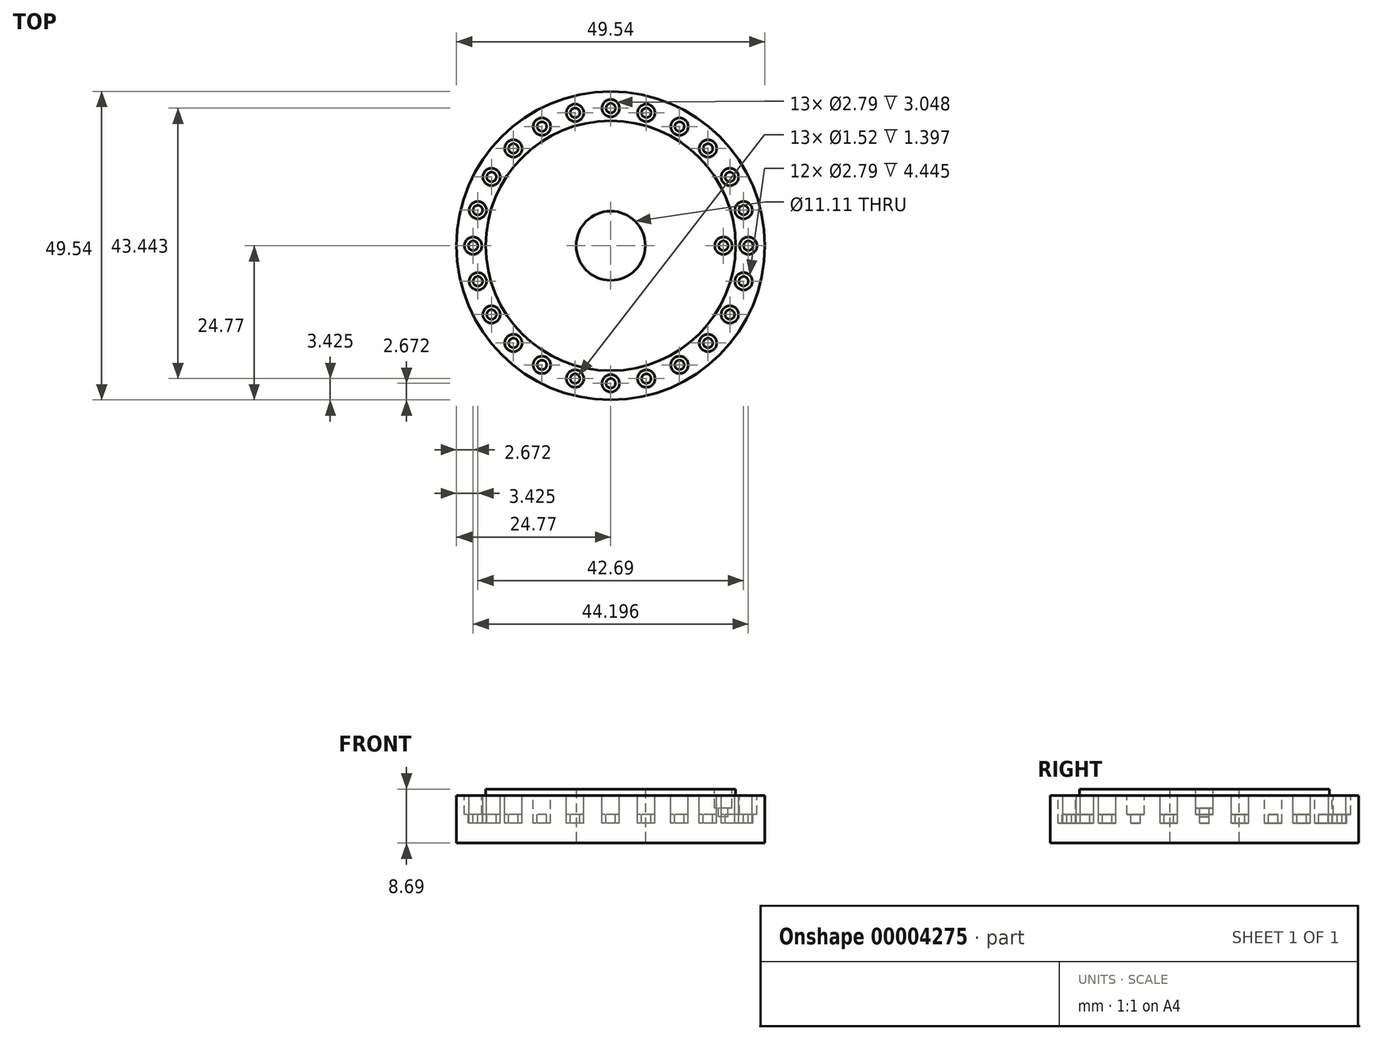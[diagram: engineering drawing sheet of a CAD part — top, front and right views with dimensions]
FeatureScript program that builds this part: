
annotation { "Feature Type Name" : "Feature", "Feature Type Description" : "" }
export const myFeature = defineFeature(function(context is Context, id is Id, definition is map)
    precondition{}
    {
        {
            var Q0;
            Q0=qCreatedBy(makeId("Top.planeOp"),FACE);
            var sketch = newSketch(context, id + "F0", { "sketchPlane" : qUnion([Q0])});
            skCircle(sketch, "E0", {"center": v(0, 0) * mm, "radius": 24.77 * mm});
            skCircle(sketch, "E1", {"center": v(0, 0) * mm, "radius": 20.07 * mm});
            skCircle(sketch, "E2", {"center": v(0, 0) * mm, "radius": 5.56 * mm});
            skSolve(sketch);
        }
        {
            var Q0;
            Q0=makeQuery(id+"F0.imprint","IMPRINT",FACE,{"disambiguationData":[TD([[makeQuery(id+"F0.imprint","IMPRINT",EDGE,{"derivedFrom":sQuery(id+"F0.wireOp",EDGE,"E1")}),1.0]])]});
            extrude(context, id + "F1", {"entities" : qUnion([Q0]), "depth" : 8.7 * mm});
        }
        {
            var Q0;
            Q0=makeQuery(id+"F0.imprint","IMPRINT",FACE,{"disambiguationData":[TD([[makeQuery(id+"F0.imprint","IMPRINT",EDGE,{"derivedFrom":sQuery(id+"F0.wireOp",EDGE,"E0")}),1.0]])]});
            extrude(context, id + "F2", {"entities" : qUnion([Q0]), "operationType" : NewBodyOperationType.ADD, "depth" : 7.62 * mm});
        }
        {
            var Q0;
            Q0=makeQuery(id+"F1.opExtrude","CAP_FACE",FACE,{"disambiguationData":[OSD([sQuery(id+"F0.wireOp",EDGE,"E1"),sQuery(id+"F0.wireOp",EDGE,"E2")])],"isStart":false});
            var sketch = newSketch(context, id + "F3", { "sketchPlane" : qUnion([Q0])});
            skLineSegment(sketch, "E3", {"start": v(0, 0) * mm, "end": v(16.71, 0) * mm});
            skCircle(sketch, "E4", {"center": v(18.11, 0) * mm, "radius": 0.76 * mm});
            skLineSegment(sketch, "E5.trimOffspring", {"start": v(19.5, 0) * mm, "end": v(20.07, 0) * mm});
            skCircle(sketch, "E6", {"center": v(18.11, 0) * mm, "radius": 1.4 * mm});
            skSolve(sketch);
        }
        {
            var Q0;
            {var subQ0=sQuery(id+"F3.wireOp",EDGE,"E4");var subQ2=makeQuery(id+"F3.imprint","INTERSECT",VERTEX,{"derivedFrom":[sQuery(id+"F3.wireOp",EDGE,"E3"),subQ0]});Q0=makeQuery(id+"F3.imprint","IMPRINT",FACE,{"disambiguationData":[TD([[makeQuery(id+"F3.imprint","IMPRINT",EDGE,{"disambiguationData":[TD([[subQ2,1.0]])],"derivedFrom":subQ0}),1.0]])]});}
            var Q1;
            Q1 = qSketchRegion(id + "F5", true);
            extrude(context, id + "F4", {"entities" : qUnion([Q0, Q1]), "operationType" : NewBodyOperationType.REMOVE, "oppositeDirection" : true, "depth" : 4.44 * mm});
        }
        {
            var Q0;
            Q0=makeQuery(id+"F2.opExtrude","CAP_FACE",FACE,{"disambiguationData":[OSD([sQuery(id+"F0.wireOp",EDGE,"E0"),sQuery(id+"F0.wireOp",EDGE,"E1")])],"isStart":false});
            var sketch = newSketch(context, id + "F5", { "sketchPlane" : qUnion([Q0])});
            skLineSegment(sketch, "E7", {"start": v(0, 0) * mm, "end": v(21.34, 0) * mm, "construction": true});
            skLineSegment(sketch, "E8", {"start": v(0, 0) * mm, "end": v(20.6, 5.52) * mm, "construction": true});
            skCircle(sketch, "E9", {"center": v(22.1, 0) * mm, "radius": 0.76 * mm});
            skCircle(sketch, "E10", {"center": v(21.35, 5.72) * mm, "radius": 0.76 * mm});
            skCircle(sketch, "E11.0.MirrorC", {"center": v(19.14, 11.05) * mm, "radius": 0.76 * mm});
            skLineSegment(sketch, "E12", {"start": v(0, 0) * mm, "end": v(18.48, 10.67) * mm, "construction": true});
            skCircle(sketch, "E13.0.MirrorC", {"center": v(15.63, 15.63) * mm, "radius": 0.76 * mm});
            skCircle(sketch, "E14.0.MirrorC", {"center": v(11.05, 19.14) * mm, "radius": 0.76 * mm});
            skLineSegment(sketch, "E15", {"start": v(0, 0) * mm, "end": v(10.67, 18.48) * mm, "construction": true});
            skCircle(sketch, "E16.0.MirrorC", {"center": v(5.72, 21.35) * mm, "radius": 0.76 * mm});
            skCircle(sketch, "E17.0.MirrorC", {"center": v(0, 22.1) * mm, "radius": 0.76 * mm});
            skCircle(sketch, "E18.0.MirrorC", {"center": v(-5.72, 21.35) * mm, "radius": 0.76 * mm});
            skCircle(sketch, "E19.0.MirrorC", {"center": v(-11.05, 19.14) * mm, "radius": 0.76 * mm});
            skLineSegment(sketch, "E20", {"start": v(0, 0) * mm, "end": v(-10.67, 18.48) * mm, "construction": true});
            skCircle(sketch, "E21.0.MirrorC", {"center": v(-15.63, 15.63) * mm, "radius": 0.76 * mm});
            skCircle(sketch, "E22.0.MirrorC", {"center": v(-19.14, 11.05) * mm, "radius": 0.76 * mm});
            skCircle(sketch, "E23.0.MirrorC", {"center": v(-21.35, 5.72) * mm, "radius": 0.76 * mm});
            skCircle(sketch, "E24.0.MirrorC", {"center": v(-22.1, 0) * mm, "radius": 0.76 * mm});
            skCircle(sketch, "E25.0.MirrorC", {"center": v(-21.35, -5.72) * mm, "radius": 0.76 * mm});
            skCircle(sketch, "E26.0.MirrorC", {"center": v(-19.14, -11.05) * mm, "radius": 0.76 * mm});
            skCircle(sketch, "E27.0.MirrorC", {"center": v(-15.63, -15.63) * mm, "radius": 0.76 * mm});
            skCircle(sketch, "E28.0.MirrorC", {"center": v(-11.05, -19.14) * mm, "radius": 0.76 * mm});
            skCircle(sketch, "E29.0.MirrorC", {"center": v(21.35, -5.72) * mm, "radius": 0.76 * mm});
            skCircle(sketch, "E30.0.MirrorC", {"center": v(19.14, -11.05) * mm, "radius": 0.76 * mm});
            skCircle(sketch, "E31.0.MirrorC", {"center": v(15.63, -15.63) * mm, "radius": 0.76 * mm});
            skCircle(sketch, "E32.0.MirrorC", {"center": v(11.05, -19.14) * mm, "radius": 0.76 * mm});
            skCircle(sketch, "E33.0.MirrorC", {"center": v(5.72, -21.35) * mm, "radius": 0.76 * mm});
            skCircle(sketch, "E34.0.MirrorC", {"center": v(0, -22.1) * mm, "radius": 0.76 * mm});
            skCircle(sketch, "E35.0.MirrorC", {"center": v(-5.72, -21.35) * mm, "radius": 0.76 * mm});
            skLineSegment(sketch, "E36.trimOffspring", {"start": v(22.08, 5.92) * mm, "end": v(23.92, 6.4) * mm, "construction": true});
            skLineSegment(sketch, "E37.trimOffspring", {"start": v(22.86, 0) * mm, "end": v(24.77, 0) * mm, "construction": true});
            skCircle(sketch, "E38", {"center": v(22.1, 0) * mm, "radius": 1.4 * mm});
            skCircle(sketch, "E39", {"center": v(21.35, 5.72) * mm, "radius": 1.4 * mm});
            skCircle(sketch, "E40", {"center": v(19.14, 11.05) * mm, "radius": 1.4 * mm});
            skCircle(sketch, "E41", {"center": v(15.63, 15.63) * mm, "radius": 1.4 * mm});
            skCircle(sketch, "E42", {"center": v(11.05, 19.14) * mm, "radius": 1.4 * mm});
            skCircle(sketch, "E43", {"center": v(5.72, 21.35) * mm, "radius": 1.4 * mm});
            skCircle(sketch, "E44", {"center": v(0, 22.1) * mm, "radius": 1.4 * mm});
            skCircle(sketch, "E45", {"center": v(-5.72, 21.35) * mm, "radius": 1.4 * mm});
            skCircle(sketch, "E46", {"center": v(-11.05, 19.14) * mm, "radius": 1.4 * mm});
            skCircle(sketch, "E47", {"center": v(-15.63, 15.63) * mm, "radius": 1.4 * mm});
            skCircle(sketch, "E48", {"center": v(-19.14, 11.05) * mm, "radius": 1.4 * mm});
            skCircle(sketch, "E49", {"center": v(-21.35, 5.72) * mm, "radius": 1.4 * mm});
            skCircle(sketch, "E50", {"center": v(-22.1, 0) * mm, "radius": 1.4 * mm});
            skCircle(sketch, "E51", {"center": v(-21.35, -5.72) * mm, "radius": 1.4 * mm});
            skCircle(sketch, "E52", {"center": v(-19.14, -11.05) * mm, "radius": 1.4 * mm});
            skCircle(sketch, "E53", {"center": v(-15.63, -15.63) * mm, "radius": 1.4 * mm});
            skCircle(sketch, "E54", {"center": v(-11.05, -19.14) * mm, "radius": 1.4 * mm});
            skCircle(sketch, "E55", {"center": v(-5.72, -21.35) * mm, "radius": 1.4 * mm});
            skCircle(sketch, "E56", {"center": v(0, -22.1) * mm, "radius": 1.4 * mm});
            skCircle(sketch, "E57", {"center": v(5.72, -21.35) * mm, "radius": 1.4 * mm});
            skCircle(sketch, "E58", {"center": v(11.05, -19.14) * mm, "radius": 1.4 * mm});
            skCircle(sketch, "E59", {"center": v(15.63, -15.63) * mm, "radius": 1.4 * mm});
            skCircle(sketch, "E60", {"center": v(19.14, -11.05) * mm, "radius": 1.4 * mm});
            skCircle(sketch, "E61", {"center": v(21.35, -5.72) * mm, "radius": 1.4 * mm});
            skSolve(sketch);
        }
        {
            var Q0;
            Q0=makeQuery(id+"F5.imprint","IMPRINT",FACE,{"disambiguationData":[TD([[makeQuery(id+"F5.imprint","IMPRINT",EDGE,{"derivedFrom":sQuery(id+"F5.wireOp",EDGE,"E9")}),1.0]])]});
            var Q1;
            Q1=makeQuery(id+"F5.imprint","IMPRINT",FACE,{"disambiguationData":[TD([[makeQuery(id+"F5.imprint","IMPRINT",EDGE,{"derivedFrom":sQuery(id+"F5.wireOp",EDGE,"E10")}),1.0]])]});
            var Q2;
            Q2=makeQuery(id+"F5.imprint","IMPRINT",FACE,{"disambiguationData":[TD([[makeQuery(id+"F5.imprint","IMPRINT",EDGE,{"derivedFrom":sQuery(id+"F5.wireOp",EDGE,"E11.0.MirrorC")}),-1.0]])]});
            var Q3;
            Q3=makeQuery(id+"F5.imprint","IMPRINT",FACE,{"disambiguationData":[TD([[makeQuery(id+"F5.imprint","IMPRINT",EDGE,{"derivedFrom":sQuery(id+"F5.wireOp",EDGE,"E13.0.MirrorC")}),-1.0]])]});
            var Q4;
            Q4=makeQuery(id+"F5.imprint","IMPRINT",FACE,{"disambiguationData":[TD([[makeQuery(id+"F5.imprint","IMPRINT",EDGE,{"derivedFrom":sQuery(id+"F5.wireOp",EDGE,"E14.0.MirrorC")}),-1.0]])]});
            var Q5;
            Q5=makeQuery(id+"F5.imprint","IMPRINT",FACE,{"disambiguationData":[TD([[makeQuery(id+"F5.imprint","IMPRINT",EDGE,{"derivedFrom":sQuery(id+"F5.wireOp",EDGE,"E16.0.MirrorC")}),1.0]])]});
            var Q6;
            Q6=makeQuery(id+"F5.imprint","IMPRINT",FACE,{"disambiguationData":[TD([[makeQuery(id+"F5.imprint","IMPRINT",EDGE,{"derivedFrom":sQuery(id+"F5.wireOp",EDGE,"E17.0.MirrorC")}),1.0]])]});
            var Q7;
            Q7=makeQuery(id+"F5.imprint","IMPRINT",FACE,{"disambiguationData":[TD([[makeQuery(id+"F5.imprint","IMPRINT",EDGE,{"derivedFrom":sQuery(id+"F5.wireOp",EDGE,"E18.0.MirrorC")}),-1.0]])]});
            var Q8;
            Q8=makeQuery(id+"F5.imprint","IMPRINT",FACE,{"disambiguationData":[TD([[makeQuery(id+"F5.imprint","IMPRINT",EDGE,{"derivedFrom":sQuery(id+"F5.wireOp",EDGE,"E19.0.MirrorC")}),-1.0]])]});
            var Q9;
            Q9=makeQuery(id+"F5.imprint","IMPRINT",FACE,{"disambiguationData":[TD([[makeQuery(id+"F5.imprint","IMPRINT",EDGE,{"derivedFrom":sQuery(id+"F5.wireOp",EDGE,"E21.0.MirrorC")}),1.0]])]});
            var Q10;
            Q10=makeQuery(id+"F5.imprint","IMPRINT",FACE,{"disambiguationData":[TD([[makeQuery(id+"F5.imprint","IMPRINT",EDGE,{"derivedFrom":sQuery(id+"F5.wireOp",EDGE,"E22.0.MirrorC")}),-1.0]])]});
            var Q11;
            Q11=makeQuery(id+"F5.imprint","IMPRINT",FACE,{"disambiguationData":[TD([[makeQuery(id+"F5.imprint","IMPRINT",EDGE,{"derivedFrom":sQuery(id+"F5.wireOp",EDGE,"E23.0.MirrorC")}),-1.0]])]});
            var Q12;
            Q12=makeQuery(id+"F5.imprint","IMPRINT",FACE,{"disambiguationData":[TD([[makeQuery(id+"F5.imprint","IMPRINT",EDGE,{"derivedFrom":sQuery(id+"F5.wireOp",EDGE,"E24.0.MirrorC")}),1.0]])]});
            var Q13;
            Q13=makeQuery(id+"F5.imprint","IMPRINT",FACE,{"disambiguationData":[TD([[makeQuery(id+"F5.imprint","IMPRINT",EDGE,{"derivedFrom":sQuery(id+"F5.wireOp",EDGE,"E25.0.MirrorC")}),1.0]])]});
            var Q14;
            Q14=makeQuery(id+"F5.imprint","IMPRINT",FACE,{"disambiguationData":[TD([[makeQuery(id+"F5.imprint","IMPRINT",EDGE,{"derivedFrom":sQuery(id+"F5.wireOp",EDGE,"E26.0.MirrorC")}),1.0]])]});
            var Q15;
            Q15=makeQuery(id+"F5.imprint","IMPRINT",FACE,{"disambiguationData":[TD([[makeQuery(id+"F5.imprint","IMPRINT",EDGE,{"derivedFrom":sQuery(id+"F5.wireOp",EDGE,"E27.0.MirrorC")}),-1.0]])]});
            var Q16;
            Q16=makeQuery(id+"F5.imprint","IMPRINT",FACE,{"disambiguationData":[TD([[makeQuery(id+"F5.imprint","IMPRINT",EDGE,{"derivedFrom":sQuery(id+"F5.wireOp",EDGE,"E28.0.MirrorC")}),-1.0]])]});
            var Q17;
            Q17=makeQuery(id+"F5.imprint","IMPRINT",FACE,{"disambiguationData":[TD([[makeQuery(id+"F5.imprint","IMPRINT",EDGE,{"derivedFrom":sQuery(id+"F5.wireOp",EDGE,"E35.0.MirrorC")}),1.0]])]});
            var Q18;
            Q18=makeQuery(id+"F5.imprint","IMPRINT",FACE,{"disambiguationData":[TD([[makeQuery(id+"F5.imprint","IMPRINT",EDGE,{"derivedFrom":sQuery(id+"F5.wireOp",EDGE,"E34.0.MirrorC")}),-1.0]])]});
            var Q19;
            Q19=makeQuery(id+"F5.imprint","IMPRINT",FACE,{"disambiguationData":[TD([[makeQuery(id+"F5.imprint","IMPRINT",EDGE,{"derivedFrom":sQuery(id+"F5.wireOp",EDGE,"E33.0.MirrorC")}),-1.0]])]});
            var Q20;
            Q20=makeQuery(id+"F5.imprint","IMPRINT",FACE,{"disambiguationData":[TD([[makeQuery(id+"F5.imprint","IMPRINT",EDGE,{"derivedFrom":sQuery(id+"F5.wireOp",EDGE,"E32.0.MirrorC")}),1.0]])]});
            var Q21;
            Q21=makeQuery(id+"F5.imprint","IMPRINT",FACE,{"disambiguationData":[TD([[makeQuery(id+"F5.imprint","IMPRINT",EDGE,{"derivedFrom":sQuery(id+"F5.wireOp",EDGE,"E31.0.MirrorC")}),1.0]])]});
            var Q22;
            Q22=makeQuery(id+"F5.imprint","IMPRINT",FACE,{"disambiguationData":[TD([[makeQuery(id+"F5.imprint","IMPRINT",EDGE,{"derivedFrom":sQuery(id+"F5.wireOp",EDGE,"E30.0.MirrorC")}),1.0]])]});
            var Q23;
            Q23=makeQuery(id+"F5.imprint","IMPRINT",FACE,{"disambiguationData":[TD([[makeQuery(id+"F5.imprint","IMPRINT",EDGE,{"derivedFrom":sQuery(id+"F5.wireOp",EDGE,"E29.0.MirrorC")}),-1.0]])]});
            extrude(context, id + "F6", {"entities" : qUnion([Q0, Q1, Q2, Q3, Q4, Q5, Q6, Q7, Q8, Q9, Q10, Q11, Q12, Q13, Q14, Q15, Q16, Q17, Q18, Q19, Q20, Q21, Q22, Q23]), "operationType" : NewBodyOperationType.REMOVE, "oppositeDirection" : true, "depth" : 4.44 * mm});
        }
        {
            var Q0;
            Q0=qSketchRegion(id+"F3",true);
            extrude(context, id + "F7", {"entities" : qUnion([Q0]), "operationType" : NewBodyOperationType.REMOVE, "oppositeDirection" : true, "depth" : 3.05 * mm});
        }
        {
            var Q0;
            Q0=makeQuery(id+"F5.imprint","IMPRINT",FACE,{"disambiguationData":[TD([[makeQuery(id+"F5.imprint","IMPRINT",EDGE,{"derivedFrom":sQuery(id+"F5.wireOp",EDGE,"E9")}),-1.0]])]});
            var Q1;
            Q1=makeQuery(id+"F5.imprint","IMPRINT",FACE,{"disambiguationData":[TD([[makeQuery(id+"F5.imprint","IMPRINT",EDGE,{"derivedFrom":sQuery(id+"F5.wireOp",EDGE,"E10")}),-1.0]])]});
            var Q2;
            Q2=makeQuery(id+"F5.imprint","IMPRINT",FACE,{"disambiguationData":[TD([[makeQuery(id+"F5.imprint","IMPRINT",EDGE,{"derivedFrom":sQuery(id+"F5.wireOp",EDGE,"E29.0.MirrorC")}),1.0]])]});
            var Q3;
            Q3=makeQuery(id+"F5.imprint","IMPRINT",FACE,{"disambiguationData":[TD([[makeQuery(id+"F5.imprint","IMPRINT",EDGE,{"derivedFrom":sQuery(id+"F5.wireOp",EDGE,"E11.0.MirrorC")}),1.0]])]});
            var Q4;
            Q4=makeQuery(id+"F5.imprint","IMPRINT",FACE,{"disambiguationData":[TD([[makeQuery(id+"F5.imprint","IMPRINT",EDGE,{"derivedFrom":sQuery(id+"F5.wireOp",EDGE,"E13.0.MirrorC")}),1.0]])]});
            var Q5;
            Q5=makeQuery(id+"F5.imprint","IMPRINT",FACE,{"disambiguationData":[TD([[makeQuery(id+"F5.imprint","IMPRINT",EDGE,{"derivedFrom":sQuery(id+"F5.wireOp",EDGE,"E14.0.MirrorC")}),1.0]])]});
            var Q6;
            Q6=makeQuery(id+"F5.imprint","IMPRINT",FACE,{"disambiguationData":[TD([[makeQuery(id+"F5.imprint","IMPRINT",EDGE,{"derivedFrom":sQuery(id+"F5.wireOp",EDGE,"E16.0.MirrorC")}),-1.0]])]});
            var Q7;
            Q7=makeQuery(id+"F5.imprint","IMPRINT",FACE,{"disambiguationData":[TD([[makeQuery(id+"F5.imprint","IMPRINT",EDGE,{"derivedFrom":sQuery(id+"F5.wireOp",EDGE,"E17.0.MirrorC")}),-1.0]])]});
            var Q8;
            Q8=makeQuery(id+"F5.imprint","IMPRINT",FACE,{"disambiguationData":[TD([[makeQuery(id+"F5.imprint","IMPRINT",EDGE,{"derivedFrom":sQuery(id+"F5.wireOp",EDGE,"E18.0.MirrorC")}),1.0]])]});
            var Q9;
            Q9=makeQuery(id+"F5.imprint","IMPRINT",FACE,{"disambiguationData":[TD([[makeQuery(id+"F5.imprint","IMPRINT",EDGE,{"derivedFrom":sQuery(id+"F5.wireOp",EDGE,"E19.0.MirrorC")}),1.0]])]});
            var Q10;
            Q10=makeQuery(id+"F5.imprint","IMPRINT",FACE,{"disambiguationData":[TD([[makeQuery(id+"F5.imprint","IMPRINT",EDGE,{"derivedFrom":sQuery(id+"F5.wireOp",EDGE,"E21.0.MirrorC")}),-1.0]])]});
            var Q11;
            Q11=makeQuery(id+"F5.imprint","IMPRINT",FACE,{"disambiguationData":[TD([[makeQuery(id+"F5.imprint","IMPRINT",EDGE,{"derivedFrom":sQuery(id+"F5.wireOp",EDGE,"E22.0.MirrorC")}),1.0]])]});
            var Q12;
            Q12=makeQuery(id+"F5.imprint","IMPRINT",FACE,{"disambiguationData":[TD([[makeQuery(id+"F5.imprint","IMPRINT",EDGE,{"derivedFrom":sQuery(id+"F5.wireOp",EDGE,"E23.0.MirrorC")}),1.0]])]});
            var Q13;
            Q13=makeQuery(id+"F5.imprint","IMPRINT",FACE,{"disambiguationData":[TD([[makeQuery(id+"F5.imprint","IMPRINT",EDGE,{"derivedFrom":sQuery(id+"F5.wireOp",EDGE,"E24.0.MirrorC")}),-1.0]])]});
            var Q14;
            Q14=makeQuery(id+"F5.imprint","IMPRINT",FACE,{"disambiguationData":[TD([[makeQuery(id+"F5.imprint","IMPRINT",EDGE,{"derivedFrom":sQuery(id+"F5.wireOp",EDGE,"E25.0.MirrorC")}),-1.0]])]});
            var Q15;
            Q15=makeQuery(id+"F5.imprint","IMPRINT",FACE,{"disambiguationData":[TD([[makeQuery(id+"F5.imprint","IMPRINT",EDGE,{"derivedFrom":sQuery(id+"F5.wireOp",EDGE,"E26.0.MirrorC")}),-1.0]])]});
            var Q16;
            Q16=makeQuery(id+"F5.imprint","IMPRINT",FACE,{"disambiguationData":[TD([[makeQuery(id+"F5.imprint","IMPRINT",EDGE,{"derivedFrom":sQuery(id+"F5.wireOp",EDGE,"E27.0.MirrorC")}),1.0]])]});
            var Q17;
            Q17=makeQuery(id+"F5.imprint","IMPRINT",FACE,{"disambiguationData":[TD([[makeQuery(id+"F5.imprint","IMPRINT",EDGE,{"derivedFrom":sQuery(id+"F5.wireOp",EDGE,"E28.0.MirrorC")}),1.0]])]});
            var Q18;
            Q18=makeQuery(id+"F5.imprint","IMPRINT",FACE,{"disambiguationData":[TD([[makeQuery(id+"F5.imprint","IMPRINT",EDGE,{"derivedFrom":sQuery(id+"F5.wireOp",EDGE,"E35.0.MirrorC")}),-1.0]])]});
            var Q19;
            Q19=makeQuery(id+"F5.imprint","IMPRINT",FACE,{"disambiguationData":[TD([[makeQuery(id+"F5.imprint","IMPRINT",EDGE,{"derivedFrom":sQuery(id+"F5.wireOp",EDGE,"E34.0.MirrorC")}),1.0]])]});
            var Q20;
            Q20=makeQuery(id+"F5.imprint","IMPRINT",FACE,{"disambiguationData":[TD([[makeQuery(id+"F5.imprint","IMPRINT",EDGE,{"derivedFrom":sQuery(id+"F5.wireOp",EDGE,"E33.0.MirrorC")}),1.0]])]});
            var Q21;
            Q21=makeQuery(id+"F5.imprint","IMPRINT",FACE,{"disambiguationData":[TD([[makeQuery(id+"F5.imprint","IMPRINT",EDGE,{"derivedFrom":sQuery(id+"F5.wireOp",EDGE,"E32.0.MirrorC")}),-1.0]])]});
            var Q22;
            Q22=makeQuery(id+"F5.imprint","IMPRINT",FACE,{"disambiguationData":[TD([[makeQuery(id+"F5.imprint","IMPRINT",EDGE,{"derivedFrom":sQuery(id+"F5.wireOp",EDGE,"E31.0.MirrorC")}),-1.0]])]});
            var Q23;
            Q23=makeQuery(id+"F5.imprint","IMPRINT",FACE,{"disambiguationData":[TD([[makeQuery(id+"F5.imprint","IMPRINT",EDGE,{"derivedFrom":sQuery(id+"F5.wireOp",EDGE,"E30.0.MirrorC")}),-1.0]])]});
            extrude(context, id + "F8", {"entities" : qUnion([Q0, Q1, Q2, Q3, Q4, Q5, Q6, Q7, Q8, Q9, Q10, Q11, Q12, Q13, Q14, Q15, Q16, Q17, Q18, Q19, Q20, Q21, Q22, Q23]), "operationType" : NewBodyOperationType.REMOVE, "oppositeDirection" : true, "depth" : 3.05 * mm});
        }
    });
